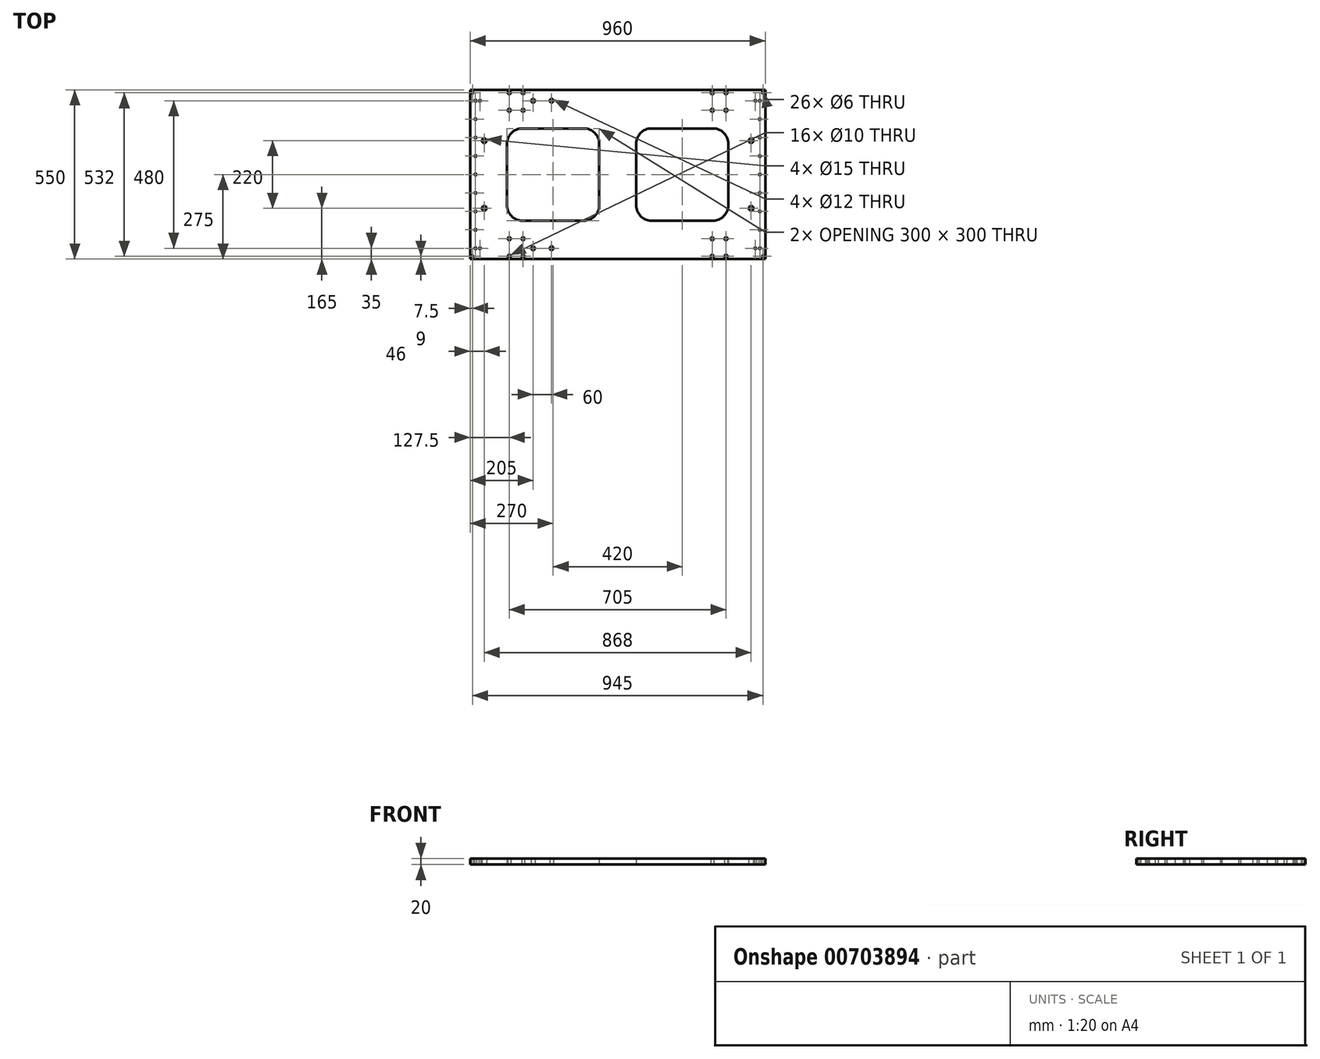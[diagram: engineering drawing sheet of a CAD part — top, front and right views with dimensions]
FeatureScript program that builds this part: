
annotation { "Feature Type Name" : "Feature", "Feature Type Description" : "" }
export const myFeature = defineFeature(function(context is Context, id is Id, definition is map)
    precondition{}
    {
        {
            var Q0;
            Q0=qCreatedBy(makeId("Top.planeOp"),FACE);
            var sketch = newSketch(context, id + "F0", { "sketchPlane" : qUnion([Q0])});
            skLineSegment(sketch, "E0.bottom", {"start": v(0, 0) * mm, "end": v(960, 0) * mm});
            skLineSegment(sketch, "E0.top", {"start": v(0, -550) * mm, "end": v(960, -550) * mm});
            skLineSegment(sketch, "E0.left", {"start": v(0, 0) * mm, "end": v(0, -550) * mm});
            skLineSegment(sketch, "E0.right", {"start": v(960, 0) * mm, "end": v(960, -550) * mm});
            skLineSegment(sketch, "E1.bottom", {"start": v(170, -125) * mm, "end": v(370, -125) * mm});
            skLineSegment(sketch, "E1.top", {"start": v(170, -425) * mm, "end": v(370, -425) * mm});
            skLineSegment(sketch, "E1.left", {"start": v(120, -175) * mm, "end": v(120, -375) * mm});
            skLineSegment(sketch, "E1.right", {"start": v(420, -175) * mm, "end": v(420, -375) * mm});
            skPoint(sketch, "E2.visualSharp", {"position": v(120, -125) * mm});
            skArc(sketch, "E2.filletArc", {"start": v(170, -125) * mm, "mid": v(134.64, -139.64) * mm, "end": v(120, -175) * mm});
            skPoint(sketch, "E3.visualSharp", {"position": v(420, -125) * mm});
            skArc(sketch, "E3.filletArc", {"start": v(420, -175) * mm, "mid": v(405.36, -139.64) * mm, "end": v(370, -125) * mm});
            skPoint(sketch, "E4.visualSharp", {"position": v(420, -425) * mm});
            skArc(sketch, "E4.filletArc", {"start": v(370, -425) * mm, "mid": v(405.36, -410.36) * mm, "end": v(420, -375) * mm});
            skPoint(sketch, "E5.visualSharp", {"position": v(120, -425) * mm});
            skArc(sketch, "E5.filletArc", {"start": v(120, -375) * mm, "mid": v(134.64, -410.36) * mm, "end": v(170, -425) * mm});
            skLineSegment(sketch, "E6.MirrorCS", {"start": v(790, -425) * mm, "end": v(590, -425) * mm});
            skArc(sketch, "E7.MirrorCS", {"start": v(790, -125) * mm, "mid": v(825.36, -139.64) * mm, "end": v(840, -175) * mm});
            skArc(sketch, "E8.MirrorCS", {"start": v(840, -375) * mm, "mid": v(825.36, -410.36) * mm, "end": v(790, -425) * mm});
            skLineSegment(sketch, "E9.MirrorCS", {"start": v(840, -175) * mm, "end": v(840, -375) * mm});
            skPoint(sketch, "E10.MirrorP", {"position": v(540, -425) * mm});
            skLineSegment(sketch, "E11.MirrorCS", {"start": v(540, -175) * mm, "end": v(540, -375) * mm});
            skArc(sketch, "E12.MirrorCS", {"start": v(540, -175) * mm, "mid": v(554.64, -139.64) * mm, "end": v(590, -125) * mm});
            skPoint(sketch, "E13.MirrorP", {"position": v(540, -125) * mm});
            skLineSegment(sketch, "E14.MirrorCS", {"start": v(790, -125) * mm, "end": v(590, -125) * mm});
            skPoint(sketch, "E15.MirrorP", {"position": v(840, -425) * mm});
            skPoint(sketch, "E16.MirrorP", {"position": v(840, -125) * mm});
            skArc(sketch, "E17.MirrorCS", {"start": v(590, -425) * mm, "mid": v(554.64, -410.36) * mm, "end": v(540, -375) * mm});
            skCircle(sketch, "E18", {"center": v(7.5, -9) * mm, "radius": 3 * mm});
            skCircle(sketch, "E19", {"center": v(17.5, -35) * mm, "radius": 3 * mm});
            skCircle(sketch, "E20", {"center": v(17.5, -95) * mm, "radius": 3 * mm});
            skCircle(sketch, "E21", {"center": v(17.5, -155) * mm, "radius": 3 * mm});
            skCircle(sketch, "E22", {"center": v(17.5, -215) * mm, "radius": 3 * mm});
            skCircle(sketch, "E23", {"center": v(17.5, -275) * mm, "radius": 3 * mm});
            skCircle(sketch, "E24.MirrorC", {"center": v(7.5, -541) * mm, "radius": 3 * mm});
            skCircle(sketch, "E25.MirrorC", {"center": v(17.5, -395) * mm, "radius": 3 * mm});
            skCircle(sketch, "E26.MirrorC", {"center": v(17.5, -335) * mm, "radius": 3 * mm});
            skCircle(sketch, "E27.MirrorC", {"center": v(17.5, -515) * mm, "radius": 3 * mm});
            skCircle(sketch, "E28.MirrorC", {"center": v(17.5, -455) * mm, "radius": 3 * mm});
            skCircle(sketch, "E29", {"center": v(32, -35) * mm, "radius": 3 * mm});
            skCircle(sketch, "E30.MirrorC", {"center": v(32, -515) * mm, "radius": 3 * mm});
            skCircle(sketch, "E31", {"center": v(46, -165) * mm, "radius": 7.5 * mm});
            skCircle(sketch, "E32.MirrorC", {"center": v(46, -385) * mm, "radius": 7.5 * mm});
            skCircle(sketch, "E33", {"center": v(127.5, -9) * mm, "radius": 5 * mm});
            skCircle(sketch, "E34", {"center": v(172.5, -9) * mm, "radius": 5 * mm});
            skCircle(sketch, "E35.MirrorC", {"center": v(172.5, -66) * mm, "radius": 5 * mm});
            skCircle(sketch, "E36.MirrorC", {"center": v(127.5, -66) * mm, "radius": 5 * mm});
            skCircle(sketch, "E37.MirrorC", {"center": v(832.5, -66) * mm, "radius": 5 * mm});
            skCircle(sketch, "E38.MirrorC", {"center": v(787.5, -9) * mm, "radius": 5 * mm});
            skCircle(sketch, "E39.MirrorC", {"center": v(787.5, -66) * mm, "radius": 5 * mm});
            skCircle(sketch, "E40.MirrorC", {"center": v(832.5, -9) * mm, "radius": 5 * mm});
            skCircle(sketch, "E41.MirrorC", {"center": v(127.5, -484) * mm, "radius": 5 * mm});
            skCircle(sketch, "E42.MirrorC", {"center": v(172.5, -484) * mm, "radius": 5 * mm});
            skCircle(sketch, "E43.MirrorC", {"center": v(127.5, -541) * mm, "radius": 5 * mm});
            skCircle(sketch, "E44.MirrorC", {"center": v(172.5, -541) * mm, "radius": 5 * mm});
            skCircle(sketch, "E45.MirrorC", {"center": v(787.5, -484) * mm, "radius": 5 * mm});
            skCircle(sketch, "E46.MirrorC", {"center": v(832.5, -541) * mm, "radius": 5 * mm});
            skCircle(sketch, "E47.MirrorC", {"center": v(832.5, -484) * mm, "radius": 5 * mm});
            skCircle(sketch, "E48.MirrorC", {"center": v(787.5, -541) * mm, "radius": 5 * mm});
            skCircle(sketch, "E49.MirrorC", {"center": v(942.5, -35) * mm, "radius": 3 * mm});
            skCircle(sketch, "E50.MirrorC", {"center": v(952.5, -9) * mm, "radius": 3 * mm});
            skCircle(sketch, "E51.MirrorC", {"center": v(942.5, -95) * mm, "radius": 3 * mm});
            skCircle(sketch, "E52.MirrorC", {"center": v(942.5, -215) * mm, "radius": 3 * mm});
            skCircle(sketch, "E53.MirrorC", {"center": v(942.5, -155) * mm, "radius": 3 * mm});
            skCircle(sketch, "E54.MirrorC", {"center": v(942.5, -275) * mm, "radius": 3 * mm});
            skCircle(sketch, "E55.MirrorC", {"center": v(928, -35) * mm, "radius": 3 * mm});
            skCircle(sketch, "E56.MirrorC", {"center": v(914, -165) * mm, "radius": 7.5 * mm});
            skCircle(sketch, "E57.MirrorC", {"center": v(942.5, -395) * mm, "radius": 3 * mm});
            skCircle(sketch, "E58.MirrorC", {"center": v(952.5, -541) * mm, "radius": 3 * mm});
            skCircle(sketch, "E59.MirrorC", {"center": v(942.5, -335) * mm, "radius": 3 * mm});
            skCircle(sketch, "E60.MirrorC", {"center": v(928, -515) * mm, "radius": 3 * mm});
            skCircle(sketch, "E61.MirrorC", {"center": v(942.5, -515) * mm, "radius": 3 * mm});
            skCircle(sketch, "E62.MirrorC", {"center": v(942.5, -455) * mm, "radius": 3 * mm});
            skCircle(sketch, "E63.MirrorC", {"center": v(914, -385) * mm, "radius": 7.5 * mm});
            skCircle(sketch, "E64", {"center": v(205, -35) * mm, "radius": 6 * mm});
            skCircle(sketch, "E65", {"center": v(265, -35) * mm, "radius": 6 * mm});
            skCircle(sketch, "E66.MirrorC", {"center": v(265, -515) * mm, "radius": 6 * mm});
            skCircle(sketch, "E67.MirrorC", {"center": v(205, -515) * mm, "radius": 6 * mm});
            skSolve(sketch);
        }
        {
            var Q0;
            Q0 = qSketchRegion(id + "F0", true);
            extrude(context, id + "F1", {"entities" : qUnion([Q0]), "depth" : 20 * mm, "offsetDistance" : 25 * mm});
        }
    });
